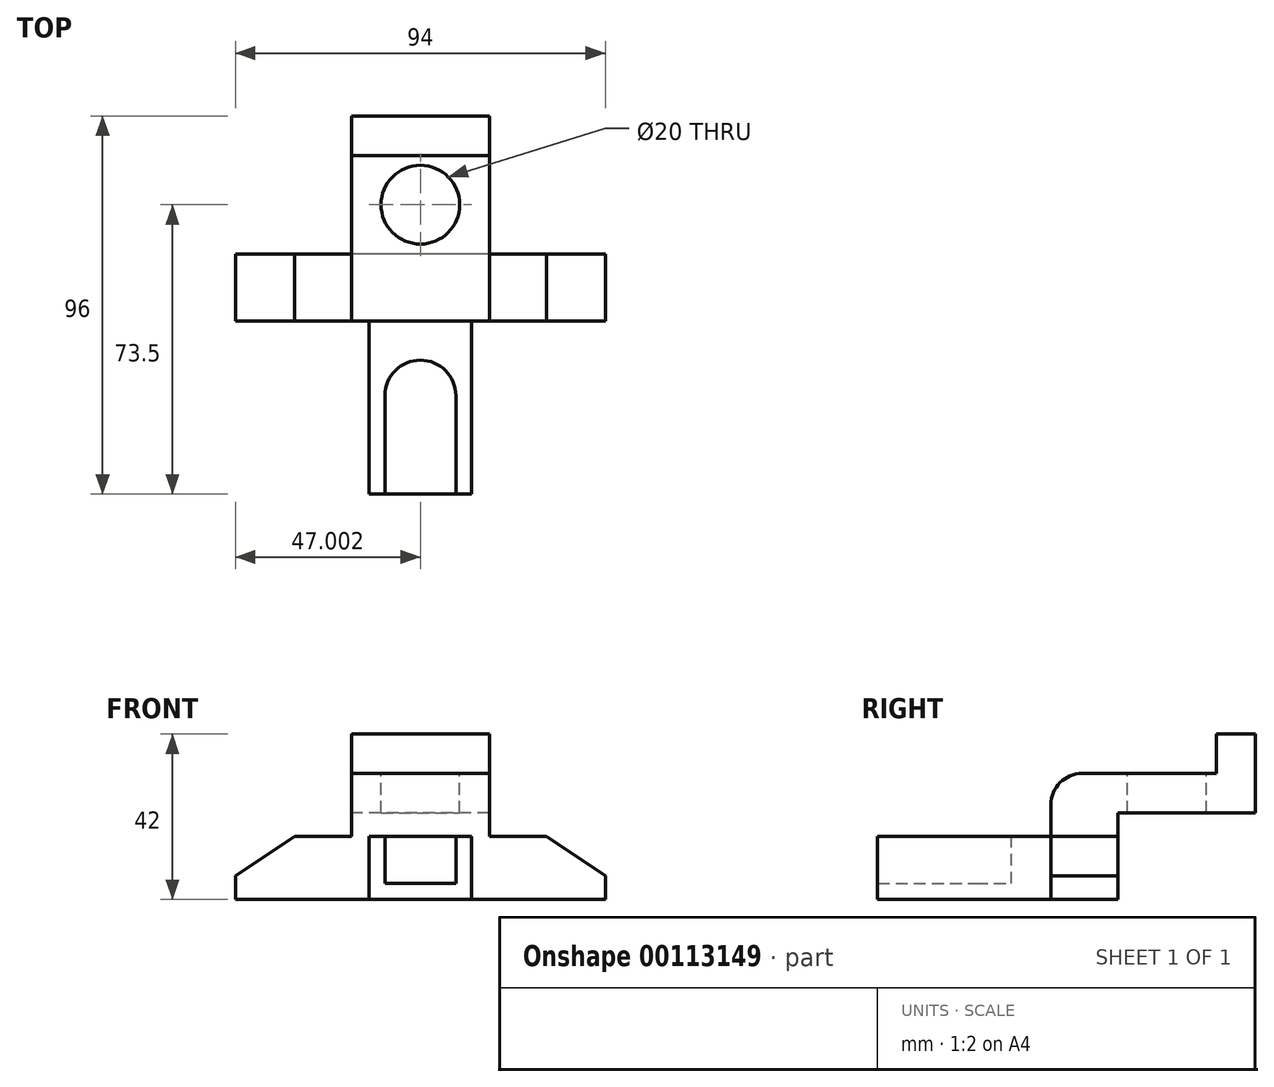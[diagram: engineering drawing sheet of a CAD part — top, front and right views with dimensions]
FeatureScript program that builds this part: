
annotation { "Feature Type Name" : "Feature", "Feature Type Description" : "" }
export const myFeature = defineFeature(function(context is Context, id is Id, definition is map)
    precondition{}
    {
        {
            var Q0;
            Q0=qCreatedBy(makeId("Front.planeOp"),FACE);
            var sketch = newSketch(context, id + "F0", { "sketchPlane" : qUnion([Q0])});
            skLineSegment(sketch, "E0.bottom", {"start": v(37.06, 29.53) * mm, "end": v(-26.94, 29.53) * mm});
            skLineSegment(sketch, "E0.top", {"start": v(52.06, 13.53) * mm, "end": v(-41.94, 13.53) * mm});
            skLineSegment(sketch, "E0.left", {"start": v(52.06, 19.53) * mm, "end": v(52.06, 13.53) * mm});
            skLineSegment(sketch, "E0.right", {"start": v(-41.94, 19.53) * mm, "end": v(-41.94, 13.53) * mm});
            skLineSegment(sketch, "E1", {"start": v(-26.94, 29.53) * mm, "end": v(-41.94, 19.53) * mm});
            skLineSegment(sketch, "E2", {"start": v(37.06, 29.53) * mm, "end": v(52.06, 19.53) * mm});
            skPoint(sketch, "E3.orphan", {"position": v(-41.94, 29.53) * mm});
            skPoint(sketch, "E4.orphan", {"position": v(52.06, 29.53) * mm});
            skSolve(sketch);
        }
        {
            var Q0;
            Q0 = qSketchRegion(id + "F0", true);
            extrude(context, id + "F1", {"entities" : qUnion([Q0]), "depth" : 17 * mm});
        }
        {
            var Q0;
            Q0=makeQuery(id+"F1.opExtrude","CAP_FACE",FACE,{"disambiguationData":[OSD([sQuery(id+"F0.wireOp",EDGE,"E0.bottom"),sQuery(id+"F0.wireOp",EDGE,"E0.top"),sQuery(id+"F0.wireOp",EDGE,"E0.left"),sQuery(id+"F0.wireOp",EDGE,"E0.right"),sQuery(id+"F0.wireOp",EDGE,"E1"),sQuery(id+"F0.wireOp",EDGE,"E2")])],"isStart":false});
            var sketch = newSketch(context, id + "F2", { "sketchPlane" : qUnion([Q0])});
            skPoint(sketch, "E5", {"position": v(5.06, 13.53) * mm});
            skLineSegment(sketch, "E6.bottom", {"start": v(-7.94, 13.53) * mm, "end": v(18.06, 13.53) * mm});
            skLineSegment(sketch, "E6.top", {"start": v(-7.94, 29.53) * mm, "end": v(18.06, 29.53) * mm});
            skLineSegment(sketch, "E6.left", {"start": v(-7.94, 13.53) * mm, "end": v(-7.94, 29.53) * mm});
            skLineSegment(sketch, "E6.right", {"start": v(18.06, 13.53) * mm, "end": v(18.06, 29.53) * mm});
            skSolve(sketch);
        }
        {
            var Q0;
            Q0 = qSketchRegion(id + "F2", true);
            extrude(context, id + "F3", {"entities" : qUnion([Q0]), "operationType" : NewBodyOperationType.ADD, "depth" : 44 * mm});
        }
        {
            var Q0;
            Q0=makeQuery(id+"F3.boolean.opBoolean","MERGE",FACE,{"derivedFrom":[makeQuery(id+"F1.opExtrude","SWEPT_FACE",FACE,{"disambiguationData":[OSD([sQuery(id+"F0.wireOp",EDGE,"E0.bottom")])]}),makeQuery(id+"F3.opExtrude","SWEPT_FACE",FACE,{"disambiguationData":[OSD([sQuery(id+"F2.wireOp",EDGE,"E6.top")])]})]});
            var sketch = newSketch(context, id + "F4", { "sketchPlane" : qUnion([Q0])});
            skLineSegment(sketch, "E7.bottom", {"start": v(14.06, -61) * mm, "end": v(-3.94, -61) * mm});
            skLineSegment(sketch, "E7.top", {"start": v(14.06, -36) * mm, "end": v(-3.94, -36) * mm});
            skLineSegment(sketch, "E7.left", {"start": v(14.06, -61) * mm, "end": v(14.06, -36) * mm});
            skLineSegment(sketch, "E7.right", {"start": v(-3.94, -61) * mm, "end": v(-3.94, -36) * mm});
            skArc(sketch, "E8", {"start": v(14.06, -36) * mm, "mid": v(5.06, -27) * mm, "end": v(-3.94, -36) * mm});
            skSolve(sketch);
        }
        {
            var Q0;
            Q0 = qSketchRegion(id + "F4", true);
            extrude(context, id + "F5", {"entities" : qUnion([Q0]), "operationType" : NewBodyOperationType.REMOVE, "oppositeDirection" : true, "depth" : 12 * mm});
        }
        {
            var Q0;
            Q0=makeQuery(id+"F1.opExtrude","SWEPT_FACE",FACE,{"disambiguationData":[OSD([sQuery(id+"F0.wireOp",EDGE,"E0.left")])]});
            cPlane(context, id + "F6", {"entities" : qUnion([Q0]), "cplaneType" : CPlaneType.OFFSET, "offset" : 47 * mm, "oppositeDirection" : true, "width" : 150 * mm, "height" : 150 * mm});
        }
        {
            var Q0;
            Q0=qCreatedBy(id+"F6.planeOp",FACE);
            var sketch = newSketch(context, id + "F7", { "sketchPlane" : qUnion([Q0])});
            skLineSegment(sketch, "E9", {"start": v(-17, 29.53) * mm, "end": v(-17, 45.53) * mm});
            skLineSegment(sketch, "E10", {"start": v(-17, 29.53) * mm, "end": v(0, 29.53) * mm});
            skLineSegment(sketch, "E11", {"start": v(-17, 45.53) * mm, "end": v(25, 45.53) * mm});
            skLineSegment(sketch, "E12", {"start": v(25, 45.53) * mm, "end": v(25, 55.53) * mm});
            skLineSegment(sketch, "E13", {"start": v(25, 55.53) * mm, "end": v(35, 55.53) * mm});
            skLineSegment(sketch, "E14", {"start": v(35, 55.53) * mm, "end": v(35, 35.53) * mm});
            skLineSegment(sketch, "E15", {"start": v(35, 35.53) * mm, "end": v(0, 35.53) * mm});
            skLineSegment(sketch, "E16", {"start": v(0, 35.53) * mm, "end": v(0, 29.53) * mm});
            skSolve(sketch);
        }
        {
            var Q0;
            Q0 = qSketchRegion(id + "F7", true);
            extrude(context, id + "F8", {"entities" : qUnion([Q0]), "operationType" : NewBodyOperationType.ADD, "endBound" : BoundingType.SYMMETRIC, "depth" : 35 * mm});
        }
        {
            var Q0;
            Q0=makeQuery(id+"F8.opExtrude","SWEPT_EDGE",EDGE,{"disambiguationData":[OSD([sQuery(id+"F7.wireOp",EDGE,"E9"),sQuery(id+"F7.wireOp",EDGE,"E11")])]});
            fillet(context, id + "F9", {"entities" : qUnion([Q0]), "radius" : 8 * mm, "tangentPropagation" : true, "allowEdgeOverflow" : false});
        }
        {
            var Q0;
            Q0=makeQuery(id+"F8.opExtrude","SWEPT_FACE",FACE,{"disambiguationData":[OSD([sQuery(id+"F7.wireOp",EDGE,"E11")])]});
            var sketch = newSketch(context, id + "F10", { "sketchPlane" : qUnion([Q0])});
            skPoint(sketch, "E17", {"position": v(5.06, -9) * mm});
            skCircle(sketch, "E18", {"center": v(5.06, 12.5) * mm, "radius": 10 * mm});
            skSolve(sketch);
        }
        {
            var Q0;
            Q0 = qSketchRegion(id + "F10", true);
            extrude(context, id + "F11", {"entities" : qUnion([Q0]), "operationType" : NewBodyOperationType.REMOVE, "oppositeDirection" : true, "depth" : 25 * mm});
        }
        {
            var Q0;
            Q0=makeQuery(id+"F8.opExtrude","SWEPT_FACE",FACE,{"disambiguationData":[OSD([sQuery(id+"F7.wireOp",EDGE,"E12")])]});
            var sketch = newSketch(context, id + "F12", { "sketchPlane" : qUnion([Q0])});
            skPoint(sketch, "E19", {"position": v(5.06, 55.53) * mm});
            skArc(sketch, "E20", {"start": v(10.12, 55.53) * mm, "mid": v(5.06, 60.6) * mm, "end": v(0, 55.53) * mm});
            skLineSegment(sketch, "E21", {"start": v(0, 55.53) * mm, "end": v(10.12, 55.53) * mm});
            skSolve(sketch);
        }
        {
            var Q0;
            Q0=makeQuery(id+"F8.opExtrude","SWEPT_FACE",FACE,{"disambiguationData":[OSD([sQuery(id+"F7.wireOp",EDGE,"E14")])]});
            var sketch = newSketch(context, id + "F13", { "sketchPlane" : qUnion([Q0])});
            skPoint(sketch, "E22", {"position": v(-5.06, 55.53) * mm});
            skArc(sketch, "E23", {"start": v(7.94, 55.53) * mm, "mid": v(-5.06, 68.53) * mm, "end": v(-18.06, 55.53) * mm});
            skLineSegment(sketch, "E24", {"start": v(-18.06, 55.53) * mm, "end": v(7.94, 55.53) * mm});
            skSolve(sketch);
        }
        {
            var Q1;
            Q1 = qSketchRegion(id + "F12", true);
            var Q2;
            Q2 = qSketchRegion(id + "F13", true);
            var Q3;
            Q3=sQuery(id+"F12.wireOp",EDGE,"E20");
            var Q4;
            Q4=sQuery(id+"F13.wireOp",EDGE,"E23");
            loft(context, id + "F14", {"bodyType" : ToolBodyType.SURFACE, "operationType" : NewBodyOperationType.ADD, "sheetProfilesArray" : [{ "sheetProfileEntities" : qUnion([Q1]) }, { "sheetProfileEntities" : qUnion([Q2]) }], "wireProfilesArray" : [{ "wireProfileEntities" : qUnion([Q3]) }, { "wireProfileEntities" : qUnion([Q4]) }]});
        }
    });
